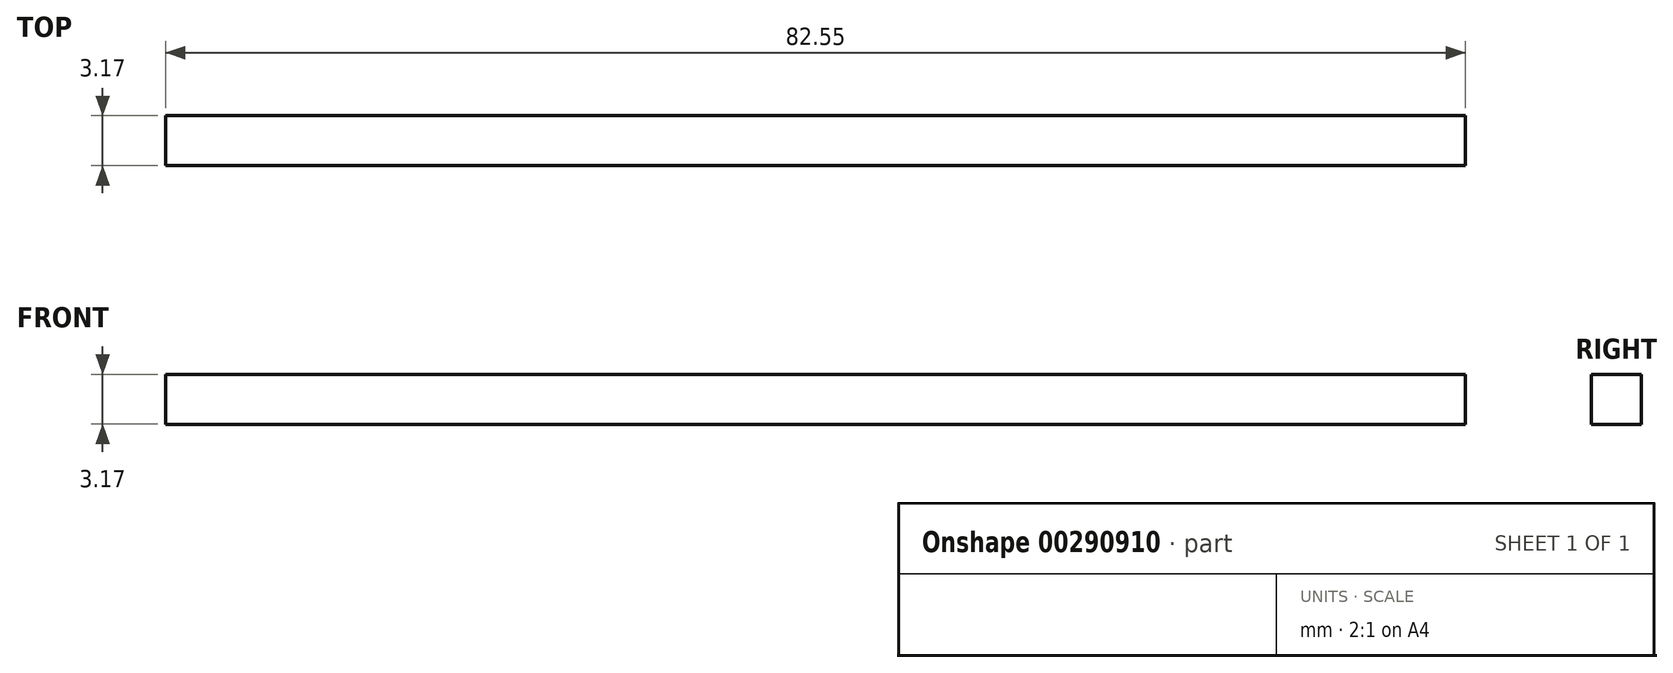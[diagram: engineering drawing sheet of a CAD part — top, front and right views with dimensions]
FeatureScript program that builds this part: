
annotation { "Feature Type Name" : "Feature", "Feature Type Description" : "" }
export const myFeature = defineFeature(function(context is Context, id is Id, definition is map)
    precondition{}
    {
        {
            var Q0;
            Q0=qCreatedBy(makeId("Front.planeOp"),FACE);
            var sketch = newSketch(context, id + "F0", { "sketchPlane" : qUnion([Q0])});
            skLineSegment(sketch, "E0.bottom", {"start": v(-54.42, 13.34) * mm, "end": v(28.13, 13.34) * mm});
            skLineSegment(sketch, "E0.top", {"start": v(-54.42, 10.17) * mm, "end": v(28.13, 10.17) * mm});
            skLineSegment(sketch, "E0.left", {"start": v(-54.42, 13.34) * mm, "end": v(-54.42, 10.17) * mm});
            skLineSegment(sketch, "E0.right", {"start": v(28.13, 13.34) * mm, "end": v(28.13, 10.17) * mm});
            skSolve(sketch);
        }
        {
            var Q0;
            Q0=qSketchRegion(id+"F0",true);
            extrude(context, id + "F1", {"entities" : qUnion([Q0]), "depth" : 3.17 * mm});
        }
    });
